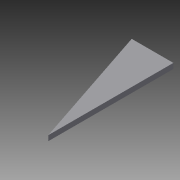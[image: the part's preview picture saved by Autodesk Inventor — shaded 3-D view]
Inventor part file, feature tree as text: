
AUTODESK INVENTOR PART (.ipt)
format: ipt  version: 2013 (Build 170138000, 138)  size: 65,024 bytes
history: native  units: in
note: dims shown in document units (in); Inventor stores cm internally (conversion verified against a paired STEP export)
features: extrude x1, sketch x1
ambient origin geometry x8: Origin, YZ Plane, XZ Plane, XY Plane, X Axis, Y Axis, Z Axis, Center Point
bodies: Solid1 (feature_tree)
feature tree (2):
  extrude  "Extrusion1"  Depth=3.0in
  sketch  "Sketch1"  dims[d0=1.0in d1=3.0in d2=0.125in d3=0.0in]
